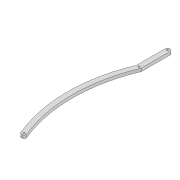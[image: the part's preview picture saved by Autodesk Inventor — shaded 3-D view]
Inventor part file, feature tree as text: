
AUTODESK INVENTOR PART (.ipt)
format: ipt  version: 2022 (Build 260153000, 153)  size: 101,376 bytes
history: native  units: mm
features: extrude x1, sketch x1
ambient origin geometry x8: Origin, YZ Plane, XZ Plane, XY Plane, X Axis, Y Axis, Z Axis, Center Point
bodies: Solid1 (feature_tree)
feature tree (2):
  extrude  "Extrusion1"  Depth=300.0mm
  sketch  "Sketch1"  dims[d0=3.3mm d1=3.3mm d2=10.0mm d3=288.984mm d6=6.0mm d7=0.0mm d14=3.3mm d15=231.585mm d16=300.0mm d17=300.0mm]
